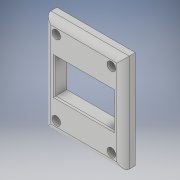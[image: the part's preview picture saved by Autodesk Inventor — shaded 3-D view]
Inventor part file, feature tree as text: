
AUTODESK INVENTOR PART (.ipt)
format: ipt  version: 2017 (Build 210142000, 142)  size: 134,656 bytes
history: native  units: in
note: dims shown in document units (in); Inventor stores cm internally (conversion verified against a paired STEP export)
features: extrude x2, sketch x2, fillet x1, chamfer x1, projected_geometry x1
ambient origin geometry x8: Origin, YZ Plane, XZ Plane, XY Plane, X Axis, Y Axis, Z Axis, Center Point
bodies: Solid1 (feature_tree)
feature tree (7):
  extrude  "Extrusion1"  Depth=1.2in
  extrude  "Extrusion2"  Depth=0.71in
  fillet  "Fillet1"  Radius=0.25in
  chamfer  "Chamfer1"  Distance=0.175in
  sketch  "Sketch1"  dims[d0=1.6in d1=1.2in]
  sketch  "Sketch2"  dims[d3=2.0in d4=0.71in d5=0.25in d6=0.0in d7=0.175in d8=0.15in d10=0.15in d11=0.15in d12=0.25in d13=0.0in d14=0.125in d15=0.025in d16=0.125in d17=45.0deg d18=0.15in]
  projected_geometry  "Projected Loop1"
